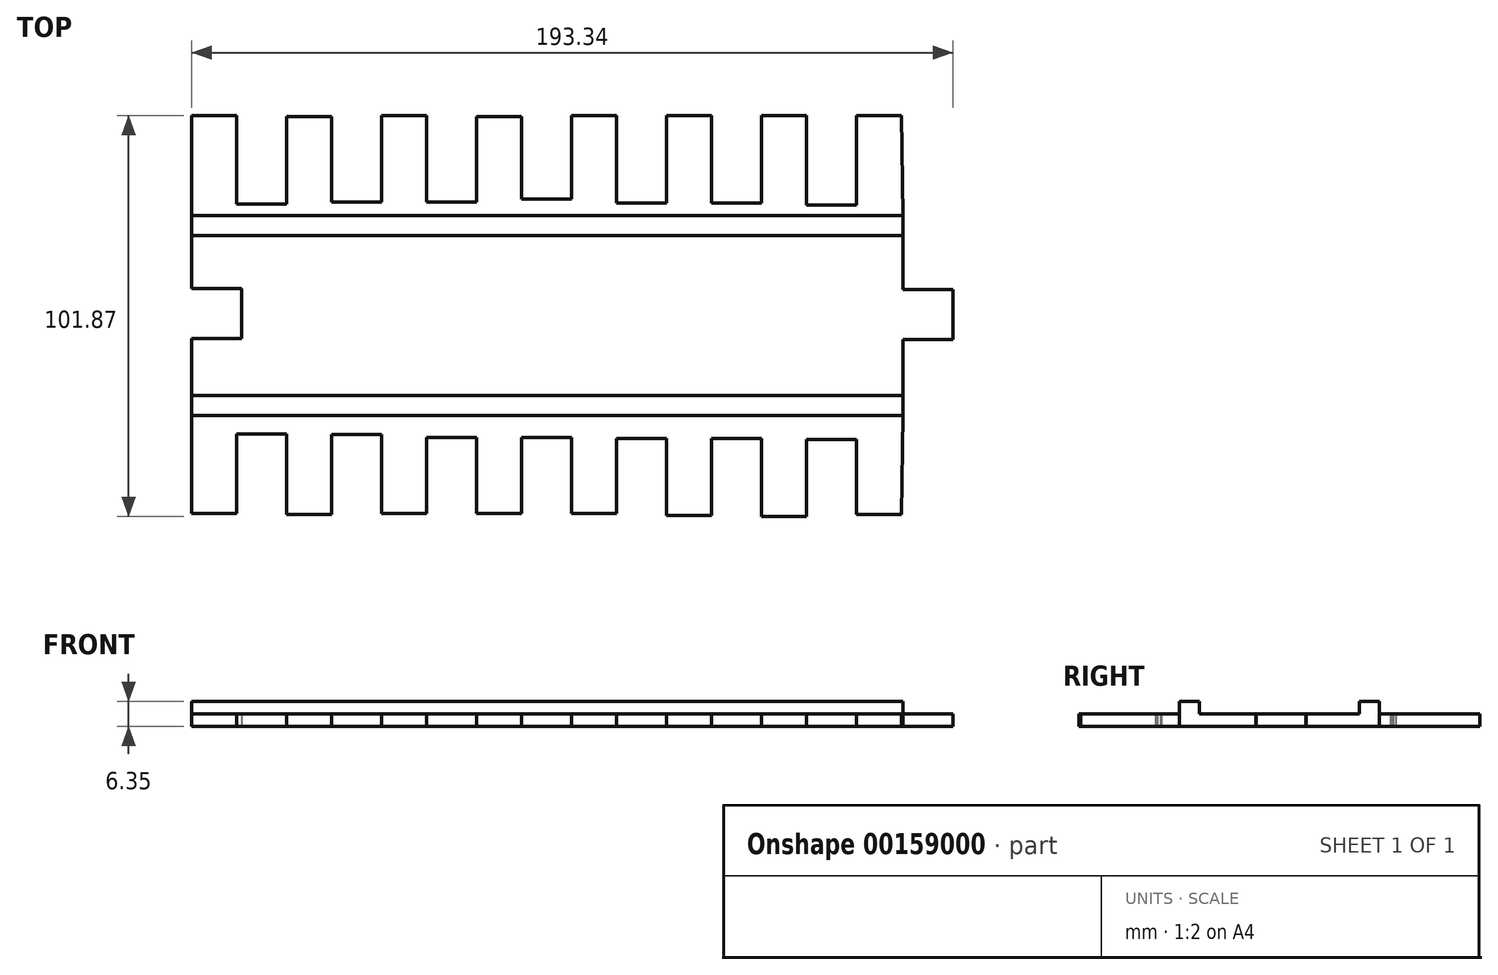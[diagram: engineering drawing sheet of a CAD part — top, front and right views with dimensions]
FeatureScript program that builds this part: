
annotation { "Feature Type Name" : "Feature", "Feature Type Description" : "" }
export const myFeature = defineFeature(function(context is Context, id is Id, definition is map)
    precondition{}
    {
        {
            var Q0;
            Q0=qCreatedBy(makeId("Top.planeOp"),FACE);
            var sketch = newSketch(context, id + "F0", { "sketchPlane" : qUnion([Q0])});
            skLineSegment(sketch, "E0.bottom", {"start": v(-7.89, 70) * mm, "end": v(172.75, 70) * mm});
            skLineSegment(sketch, "E0.top", {"start": v(-7.89, 19.2) * mm, "end": v(172.75, 19.2) * mm});
            skLineSegment(sketch, "E0.left", {"start": v(-7.89, 70) * mm, "end": v(-7.89, 19.2) * mm});
            skLineSegment(sketch, "E0.right", {"start": v(172.75, 70) * mm, "end": v(172.75, 19.2) * mm});
            skLineSegment(sketch, "E1", {"start": v(185.45, 45.14) * mm, "end": v(185.45, 38.59) * mm});
            skLineSegment(sketch, "E2", {"start": v(185.45, 38.59) * mm, "end": v(172.75, 38.59) * mm});
            skLineSegment(sketch, "E3", {"start": v(185.45, 45.14) * mm, "end": v(185.45, 51.29) * mm});
            skLineSegment(sketch, "E4", {"start": v(185.45, 51.29) * mm, "end": v(172.75, 51.29) * mm});
            skLineSegment(sketch, "E5", {"start": v(4.81, 45.14) * mm, "end": v(4.81, 51.5) * mm});
            skLineSegment(sketch, "E6", {"start": v(4.81, 51.5) * mm, "end": v(-7.89, 51.5) * mm});
            skLineSegment(sketch, "E7", {"start": v(4.81, 45.14) * mm, "end": v(4.81, 38.8) * mm});
            skLineSegment(sketch, "E8", {"start": v(4.81, 38.8) * mm, "end": v(-7.89, 38.8) * mm});
            skLineSegment(sketch, "E9", {"start": v(4.81, 38.8) * mm, "end": v(4.81, 51.5) * mm});
            skLineSegment(sketch, "E10", {"start": v(-7.89, 64.92) * mm, "end": v(172.75, 64.92) * mm});
            skLineSegment(sketch, "E11", {"start": v(172.75, 24.28) * mm, "end": v(-7.89, 24.28) * mm});
            skLineSegment(sketch, "E12", {"start": v(-7.89, 64.92) * mm, "end": v(-7.89, 70) * mm});
            skLineSegment(sketch, "E13", {"start": v(-7.89, 70) * mm, "end": v(-7.89, 95.4) * mm});
            skLineSegment(sketch, "E14", {"start": v(-7.89, 95.4) * mm, "end": v(3.54, 95.4) * mm});
            skLineSegment(sketch, "E15", {"start": v(3.54, 95.4) * mm, "end": v(3.54, 72.97) * mm});
            skLineSegment(sketch, "E16", {"start": v(3.54, 72.97) * mm, "end": v(16.24, 72.97) * mm});
            skLineSegment(sketch, "E17", {"start": v(16.24, 72.97) * mm, "end": v(16.24, 95.2) * mm});
            skLineSegment(sketch, "E18", {"start": v(16.24, 95.2) * mm, "end": v(27.67, 95.2) * mm});
            skLineSegment(sketch, "E19", {"start": v(27.67, 95.2) * mm, "end": v(27.67, 73.46) * mm});
            skLineSegment(sketch, "E20", {"start": v(27.67, 73.46) * mm, "end": v(40.37, 73.46) * mm});
            skLineSegment(sketch, "E21", {"start": v(40.37, 73.46) * mm, "end": v(40.37, 95.45) * mm});
            skLineSegment(sketch, "E22", {"start": v(40.37, 95.45) * mm, "end": v(51.8, 95.45) * mm});
            skLineSegment(sketch, "E23", {"start": v(51.8, 95.45) * mm, "end": v(51.8, 73.46) * mm});
            skLineSegment(sketch, "E24", {"start": v(51.8, 73.46) * mm, "end": v(64.5, 73.46) * mm});
            skLineSegment(sketch, "E25", {"start": v(64.5, 73.46) * mm, "end": v(64.5, 95.2) * mm});
            skLineSegment(sketch, "E26", {"start": v(64.5, 95.2) * mm, "end": v(75.93, 95.2) * mm});
            skLineSegment(sketch, "E27", {"start": v(75.93, 95.2) * mm, "end": v(75.93, 74.2) * mm});
            skLineSegment(sketch, "E28", {"start": v(75.93, 74.2) * mm, "end": v(88.63, 74.2) * mm});
            skLineSegment(sketch, "E29", {"start": v(88.63, 74.2) * mm, "end": v(88.63, 95.45) * mm});
            skLineSegment(sketch, "E30", {"start": v(88.63, 95.45) * mm, "end": v(100.06, 95.45) * mm});
            skLineSegment(sketch, "E31", {"start": v(100.06, 95.45) * mm, "end": v(100.06, 73.21) * mm});
            skLineSegment(sketch, "E32", {"start": v(100.06, 73.21) * mm, "end": v(112.76, 73.21) * mm});
            skLineSegment(sketch, "E33", {"start": v(112.76, 73.21) * mm, "end": v(112.76, 95.45) * mm});
            skLineSegment(sketch, "E34", {"start": v(112.76, 95.45) * mm, "end": v(124.2, 95.45) * mm});
            skLineSegment(sketch, "E35", {"start": v(124.2, 95.45) * mm, "end": v(124.2, 73.21) * mm});
            skLineSegment(sketch, "E36", {"start": v(124.2, 73.21) * mm, "end": v(136.9, 73.21) * mm});
            skLineSegment(sketch, "E37", {"start": v(136.9, 73.21) * mm, "end": v(136.9, 95.45) * mm});
            skLineSegment(sketch, "E38", {"start": v(136.9, 95.45) * mm, "end": v(148.32, 95.45) * mm});
            skLineSegment(sketch, "E39", {"start": v(148.32, 95.45) * mm, "end": v(148.32, 72.73) * mm});
            skLineSegment(sketch, "E40", {"start": v(148.32, 72.73) * mm, "end": v(161.02, 72.73) * mm});
            skLineSegment(sketch, "E41", {"start": v(161.02, 72.73) * mm, "end": v(161.02, 95.45) * mm});
            skLineSegment(sketch, "E42", {"start": v(161.02, 95.45) * mm, "end": v(172.45, 95.45) * mm});
            skLineSegment(sketch, "E43", {"start": v(172.45, 95.45) * mm, "end": v(172.75, 70) * mm});
            skLineSegment(sketch, "E44", {"start": v(-7.89, 19.2) * mm, "end": v(-7.89, -5.69) * mm});
            skLineSegment(sketch, "E45", {"start": v(-7.89, -5.69) * mm, "end": v(3.54, -5.69) * mm});
            skLineSegment(sketch, "E46", {"start": v(3.54, -5.69) * mm, "end": v(3.54, 14.59) * mm});
            skLineSegment(sketch, "E47", {"start": v(3.54, 14.59) * mm, "end": v(16.24, 14.59) * mm});
            skLineSegment(sketch, "E48", {"start": v(16.24, 14.59) * mm, "end": v(16.24, -5.93) * mm});
            skLineSegment(sketch, "E49", {"start": v(16.24, -5.93) * mm, "end": v(27.67, -5.93) * mm});
            skLineSegment(sketch, "E50", {"start": v(27.67, -5.93) * mm, "end": v(27.67, 14.35) * mm});
            skLineSegment(sketch, "E51", {"start": v(27.67, 14.35) * mm, "end": v(40.37, 14.35) * mm});
            skLineSegment(sketch, "E52", {"start": v(40.37, 14.35) * mm, "end": v(40.37, -5.69) * mm});
            skLineSegment(sketch, "E53", {"start": v(40.37, -5.69) * mm, "end": v(51.8, -5.69) * mm});
            skLineSegment(sketch, "E54", {"start": v(51.8, -5.69) * mm, "end": v(51.8, 13.61) * mm});
            skLineSegment(sketch, "E55", {"start": v(51.8, 13.61) * mm, "end": v(64.5, 13.61) * mm});
            skLineSegment(sketch, "E56", {"start": v(64.5, 13.61) * mm, "end": v(64.5, -5.69) * mm});
            skLineSegment(sketch, "E57", {"start": v(64.5, -5.69) * mm, "end": v(75.93, -5.69) * mm});
            skLineSegment(sketch, "E58", {"start": v(75.93, -5.69) * mm, "end": v(75.93, 13.61) * mm});
            skLineSegment(sketch, "E59", {"start": v(75.93, 13.61) * mm, "end": v(88.63, 13.61) * mm});
            skLineSegment(sketch, "E60", {"start": v(88.63, 13.61) * mm, "end": v(88.63, -5.69) * mm});
            skLineSegment(sketch, "E61", {"start": v(88.63, -5.69) * mm, "end": v(100.06, -5.69) * mm});
            skLineSegment(sketch, "E62", {"start": v(100.06, -5.69) * mm, "end": v(100.06, 13.37) * mm});
            skLineSegment(sketch, "E63", {"start": v(100.06, 13.37) * mm, "end": v(112.76, 13.37) * mm});
            skLineSegment(sketch, "E64", {"start": v(112.76, 13.37) * mm, "end": v(112.76, -6.18) * mm});
            skLineSegment(sketch, "E65", {"start": v(112.76, -6.18) * mm, "end": v(124.2, -6.18) * mm});
            skLineSegment(sketch, "E66", {"start": v(124.2, -6.18) * mm, "end": v(124.2, 13.37) * mm});
            skLineSegment(sketch, "E67", {"start": v(124.2, 13.37) * mm, "end": v(136.9, 13.37) * mm});
            skLineSegment(sketch, "E68", {"start": v(136.9, 13.37) * mm, "end": v(136.9, -6.42) * mm});
            skLineSegment(sketch, "E69", {"start": v(136.9, -6.42) * mm, "end": v(148.32, -6.42) * mm});
            skLineSegment(sketch, "E70", {"start": v(148.32, -6.42) * mm, "end": v(148.32, 13.12) * mm});
            skLineSegment(sketch, "E71", {"start": v(148.32, 13.12) * mm, "end": v(161.02, 13.12) * mm});
            skLineSegment(sketch, "E72", {"start": v(161.02, 13.12) * mm, "end": v(161.02, -5.93) * mm});
            skLineSegment(sketch, "E73", {"start": v(161.02, -5.93) * mm, "end": v(172.45, -5.93) * mm});
            skLineSegment(sketch, "E74", {"start": v(172.45, -5.93) * mm, "end": v(172.75, 19.2) * mm});
            skSolve(sketch);
        }
        {
            var Q0;
            Q0=makeQuery(id+"F0.imprint","IMPRINT",FACE,{"disambiguationData":[TD([[makeQuery(id+"F0.imprint","IMPRINT",EDGE,{"derivedFrom":sQuery(id+"F0.wireOp",EDGE,"E1")}),-1.0]])]});
            var Q1;
            {var subQ7=sQuery(id+"F0.wireOp",EDGE,"E6");Q1=makeQuery(id+"F0.imprint","IMPRINT",FACE,{"disambiguationData":[TD([[makeQuery(id+"F0.imprint","IMPRINT",EDGE,{"derivedFrom":subQ7}),-1.0]])]});}
            extrude(context, id + "F1", {"entities" : qUnion([Q0, Q1]), "depth" : 3.17 * mm});
        }
        {
            var Q0;
            {var subQ0=sQuery(id+"F0.wireOp",EDGE,"E0.top");Q0=makeQuery(id+"F0.imprint","IMPRINT",FACE,{"disambiguationData":[TD([[makeQuery(id+"F0.imprint","IMPRINT",EDGE,{"derivedFrom":subQ0}),1.0]])]});}
            var Q1;
            {var subQ0=sQuery(id+"F0.wireOp",EDGE,"E0.bottom");Q1=makeQuery(id+"F0.imprint","IMPRINT",FACE,{"disambiguationData":[TD([[makeQuery(id+"F0.imprint","IMPRINT",EDGE,{"derivedFrom":subQ0}),-1.0]])]});}
            extrude(context, id + "F2", {"entities" : qUnion([Q0, Q1]), "operationType" : NewBodyOperationType.ADD, "depth" : 6.35 * mm});
        }
        {
            var Q0;
            {var subQ1=sQuery(id+"F0.wireOp",EDGE,"E0.bottom");Q0=makeQuery(id+"F0.imprint","IMPRINT",FACE,{"disambiguationData":[TD([[makeQuery(id+"F0.imprint","IMPRINT",EDGE,{"derivedFrom":subQ1}),1.0]])]});}
            var Q1;
            Q1=makeQuery(id+"F0.imprint","IMPRINT",FACE,{"disambiguationData":[TD([[makeQuery(id+"F0.imprint","IMPRINT",EDGE,{"derivedFrom":sQuery(id+"F0.wireOp",EDGE,"E0.top")}),-1.0]])]});
            extrude(context, id + "F3", {"entities" : qUnion([Q0, Q1]), "operationType" : NewBodyOperationType.ADD, "depth" : 3.17 * mm});
        }
        {
            var Q0;
            Q0 = qSketchRegion(id + "F0", true);
            extrude(context, id + "F4", {"entities" : qUnion([Q0]), "operationType" : NewBodyOperationType.ADD, "depth" : 3.17 * mm});
        }
        {
            var Q0;
            {var subQ0=sQuery(id+"F0.wireOp",EDGE,"E6");Q0=makeQuery(id+"F0.imprint","IMPRINT",FACE,{"disambiguationData":[TD([[makeQuery(id+"F0.imprint","IMPRINT",EDGE,{"derivedFrom":subQ0}),1.0]])]});}
            extrude(context, id + "F5", {"entities" : qUnion([Q0]), "operationType" : NewBodyOperationType.REMOVE, "depth" : 20.32 * mm});
        }
    });
